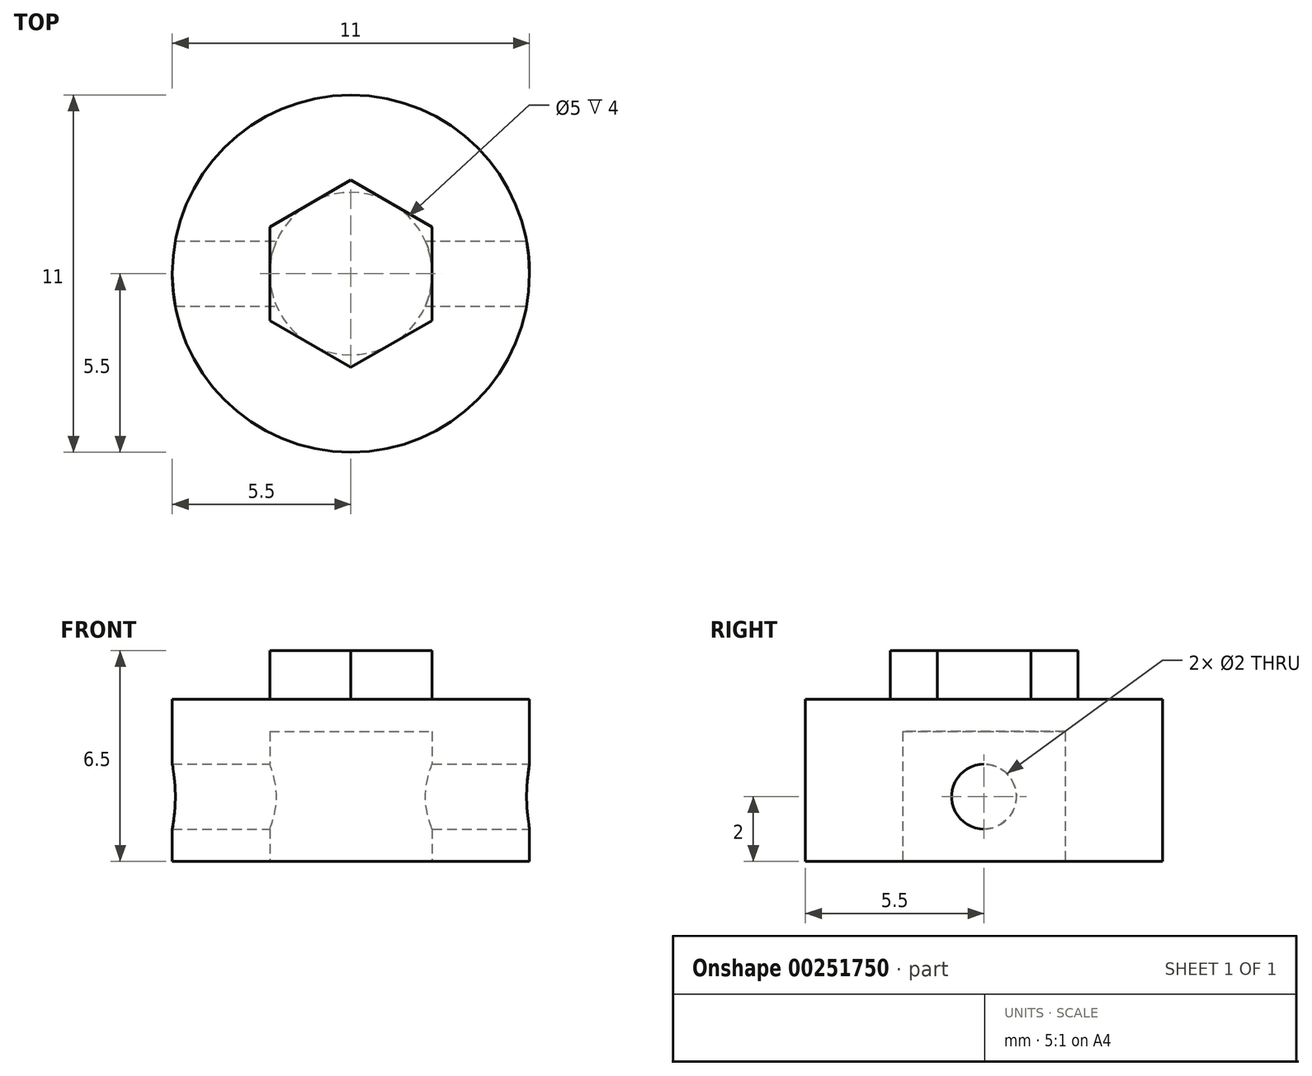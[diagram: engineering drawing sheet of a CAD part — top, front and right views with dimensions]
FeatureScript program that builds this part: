
annotation { "Feature Type Name" : "Feature", "Feature Type Description" : "" }
export const myFeature = defineFeature(function(context is Context, id is Id, definition is map)
    precondition{}
    {
        {
            var Q0;
            Q0=qCreatedBy(makeId("Top.planeOp"),FACE);
            var sketch = newSketch(context, id + "F0", { "sketchPlane" : qUnion([Q0])});
            skCircle(sketch, "E0", {"center": v(0, 0) * mm, "radius": 5.5 * mm});
            skSolve(sketch);
        }
        {
            var Q0;
            Q0 = qSketchRegion(id + "F0", true);
            extrude(context, id + "F1", {"entities" : qUnion([Q0]), "endBound" : BoundingType.SYMMETRIC, "depth" : 5 * mm});
        }
        {
            var Q0;
            Q0=qCreatedBy(makeId("Top.planeOp"),FACE);
            var sketch = newSketch(context, id + "F2", { "sketchPlane" : qUnion([Q0])});
            skCircle(sketch, "E1.cCircle", {"center": v(0, 0) * mm, "radius": 2.5 * mm, "construction": true});
            skLineSegment(sketch, "E1.0", {"start": v(0, -2.89) * mm, "end": v(-2.5, -1.44) * mm});
            skLineSegment(sketch, "E1.1", {"start": v(-2.5, -1.44) * mm, "end": v(-2.5, 1.44) * mm});
            skLineSegment(sketch, "E1.2", {"start": v(-2.5, 1.44) * mm, "end": v(0, 2.89) * mm});
            skLineSegment(sketch, "E1.3", {"start": v(0, 2.89) * mm, "end": v(2.5, 1.44) * mm});
            skLineSegment(sketch, "E1.4", {"start": v(2.5, 1.44) * mm, "end": v(2.5, -1.44) * mm});
            skLineSegment(sketch, "E1.5", {"start": v(2.5, -1.44) * mm, "end": v(0, -2.89) * mm});
            skPoint(sketch, "E1.0.midPoint", {"position": v(-1.25, -2.17) * mm});
            skSolve(sketch);
        }
        {
            var Q0;
            Q0 = qSketchRegion(id + "F2", true);
            extrude(context, id + "F3", {"entities" : qUnion([Q0]), "operationType" : NewBodyOperationType.ADD, "depth" : 4 * mm});
        }
        {
            var Q0;
            Q0=qCreatedBy(makeId("Right.planeOp"),FACE);
            var sketch = newSketch(context, id + "F4", { "sketchPlane" : qUnion([Q0])});
            skCircle(sketch, "E2", {"center": v(0, -0.5) * mm, "radius": 1 * mm});
            skSolve(sketch);
        }
        {
            var Q0;
            Q0 = qSketchRegion(id + "F4", true);
            extrude(context, id + "F5", {"entities" : qUnion([Q0]), "operationType" : NewBodyOperationType.REMOVE, "endBound" : BoundingType.SYMMETRIC, "oppositeDirection" : true, "depth" : 100 * mm});
        }
        {
            var Q0;
            Q0=makeQuery(id+"F1.opExtrude","CAP_FACE",FACE,{"disambiguationData":[OSD([sQuery(id+"F0.wireOp",EDGE,"E0")])],"isStart":true});
            var sketch = newSketch(context, id + "F6", { "sketchPlane" : qUnion([Q0])});
            skCircle(sketch, "E3", {"center": v(0, 0) * mm, "radius": 2.5 * mm});
            skSolve(sketch);
        }
        {
            var Q0;
            Q0 = qSketchRegion(id + "F6", true);
            extrude(context, id + "F7", {"entities" : qUnion([Q0]), "operationType" : NewBodyOperationType.REMOVE, "oppositeDirection" : true, "depth" : 4 * mm});
        }
    });
